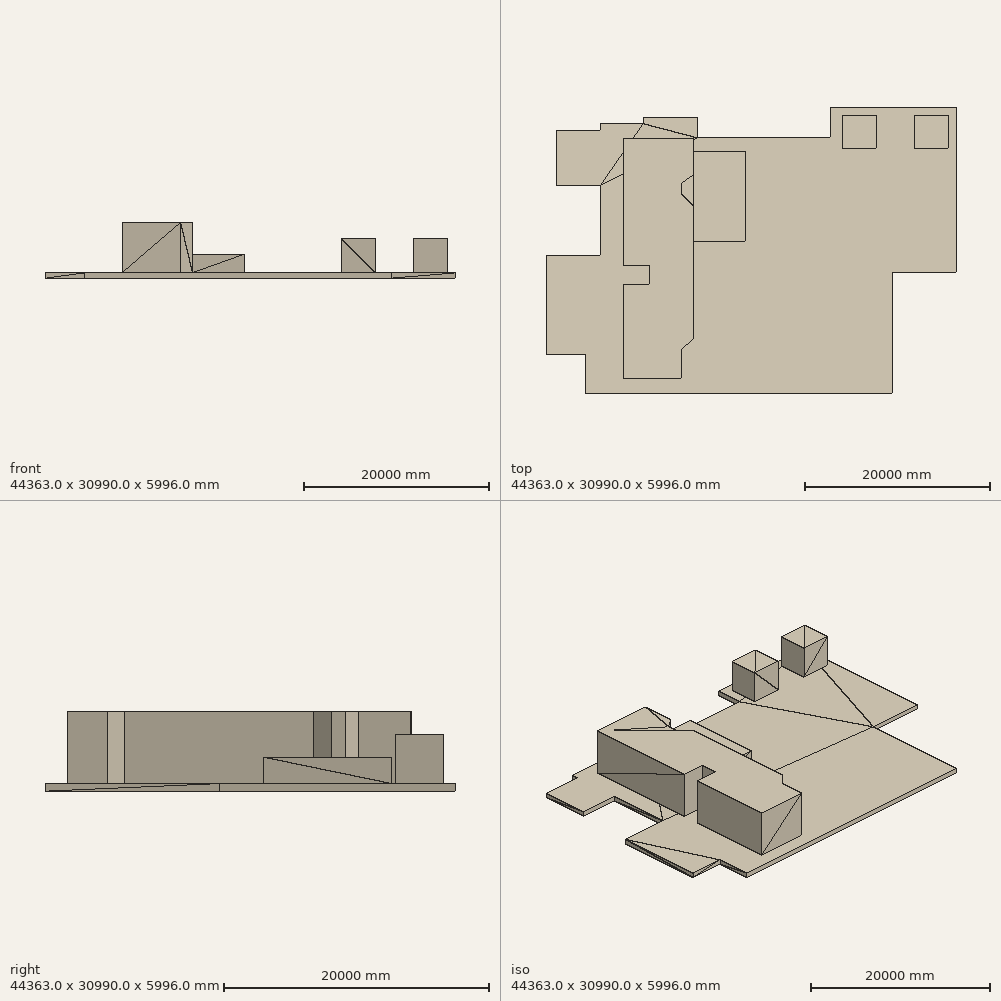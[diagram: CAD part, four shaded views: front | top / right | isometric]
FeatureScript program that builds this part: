
annotation { "Feature Type Name" : "Feature", "Feature Type Description" : "" }
export const myFeature = defineFeature(function(context is Context, id is Id, definition is map)
    precondition{}
    {
        {
            var Q0;
            Q0=qCreatedBy(makeId("Top.planeOp"),FACE);
            var sketch = newSketch(context, id + "F0", { "sketchPlane" : qUnion([Q0])});
            skLineSegment(sketch, "E0", {"start": v(0, 0) * mm, "end": v(39260, 0) * mm, "construction": true});
            skLineSegment(sketch, "E1", {"start": v(0, 0) * mm, "end": v(0, 30290) * mm, "construction": true});
            skLineSegment(sketch, "E2", {"start": v(0, 30290) * mm, "end": v(43730, 30290) * mm, "construction": true});
            skLineSegment(sketch, "E3", {"start": v(6110, 0) * mm, "end": v(39260, 0) * mm});
            skLineSegment(sketch, "E4", {"start": v(39260, 0) * mm, "end": v(39260, 13140) * mm});
            skLineSegment(sketch, "E5", {"start": v(39260, 13140) * mm, "end": v(46240, 13140) * mm});
            skLineSegment(sketch, "E6", {"start": v(46240, 13140) * mm, "end": v(46240, 30990) * mm});
            skLineSegment(sketch, "E7", {"start": v(46240, 30990) * mm, "end": v(32650, 30990) * mm});
            skLineSegment(sketch, "E8", {"start": v(32650, 30990) * mm, "end": v(32650, 27672) * mm});
            skLineSegment(sketch, "E9", {"start": v(32650, 27672) * mm, "end": v(18217, 27672) * mm});
            skLineSegment(sketch, "E10", {"start": v(18217, 27672) * mm, "end": v(18217, 29872) * mm});
            skLineSegment(sketch, "E11", {"start": v(18217, 29872) * mm, "end": v(12367, 29872) * mm});
            skLineSegment(sketch, "E12", {"start": v(12367, 29872) * mm, "end": v(12367, 29207) * mm});
            skLineSegment(sketch, "E13", {"start": v(12367, 29207) * mm, "end": v(7764, 29207) * mm});
            skLineSegment(sketch, "E14", {"start": v(7764, 29207) * mm, "end": v(7764, 28479) * mm});
            skLineSegment(sketch, "E15", {"start": v(7764, 28479) * mm, "end": v(2917, 28479) * mm});
            skLineSegment(sketch, "E16", {"start": v(2917, 28479) * mm, "end": v(2917, 22579) * mm});
            skLineSegment(sketch, "E17", {"start": v(2917, 22579) * mm, "end": v(7764, 22579) * mm});
            skLineSegment(sketch, "E18", {"start": v(7764, 22579) * mm, "end": v(7764, 14932) * mm});
            skLineSegment(sketch, "E19", {"start": v(7764, 14932) * mm, "end": v(1877, 14932) * mm});
            skLineSegment(sketch, "E20", {"start": v(1877, 14932) * mm, "end": v(1877, 4229) * mm});
            skLineSegment(sketch, "E21", {"start": v(1877, 4229) * mm, "end": v(6110, 4229) * mm});
            skLineSegment(sketch, "E22", {"start": v(6110, 4229) * mm, "end": v(6110, 0) * mm});
            skSolve(sketch);
        }
        {
            var Q0;
            Q0=makeQuery(id+"F0.imprint","IMPRINT",FACE,{"disambiguationData":[TD([[makeQuery(id+"F0.imprint","IMPRINT",EDGE,{"derivedFrom":sQuery(id+"F0.wireOp",EDGE,"E3")}),1.0]])]});
            extrude(context, id + "F1", {"entities" : qUnion([Q0]), "depth" : 570 * mm, "offsetDistance" : 25 * mm});
        }
        {
            var Q0;
            Q0=makeQuery(id+"F1.opExtrude","CAP_FACE",FACE,{"disambiguationData":[OSD([sQuery(id+"F0.wireOp",EDGE,"E3"),sQuery(id+"F0.wireOp",EDGE,"E4"),sQuery(id+"F0.wireOp",EDGE,"E5"),sQuery(id+"F0.wireOp",EDGE,"E6"),sQuery(id+"F0.wireOp",EDGE,"E7"),sQuery(id+"F0.wireOp",EDGE,"E8"),sQuery(id+"F0.wireOp",EDGE,"E9"),sQuery(id+"F0.wireOp",EDGE,"E10"),sQuery(id+"F0.wireOp",EDGE,"E11"),sQuery(id+"F0.wireOp",EDGE,"E12"),sQuery(id+"F0.wireOp",EDGE,"E13"),sQuery(id+"F0.wireOp",EDGE,"E14"),sQuery(id+"F0.wireOp",EDGE,"E15"),sQuery(id+"F0.wireOp",EDGE,"E16"),sQuery(id+"F0.wireOp",EDGE,"E17"),sQuery(id+"F0.wireOp",EDGE,"E18"),sQuery(id+"F0.wireOp",EDGE,"E19"),sQuery(id+"F0.wireOp",EDGE,"E20"),sQuery(id+"F0.wireOp",EDGE,"E21"),sQuery(id+"F0.wireOp",EDGE,"E22")])],"isStart":false});
            var sketch = newSketch(context, id + "F2", { "sketchPlane" : qUnion([Q0])});
            skLineSegment(sketch, "E23", {"start": v(0, 0) * mm, "end": v(10434, 0) * mm, "construction": true});
            skLineSegment(sketch, "E24", {"start": v(10434, 0) * mm, "end": v(10434, 1929) * mm, "construction": true});
            skLineSegment(sketch, "E25", {"start": v(16245, 4705) * mm, "end": v(17545, 4705) * mm, "construction": true});
            skLineSegment(sketch, "E26", {"start": v(17545, 4705) * mm, "end": v(17545, 5970) * mm, "construction": true});
            skLineSegment(sketch, "E27", {"start": v(17545, 20175) * mm, "end": v(16195, 20175) * mm, "construction": true});
            skLineSegment(sketch, "E28", {"start": v(16195, 20175) * mm, "end": v(16195, 21500) * mm, "construction": true});
            skLineSegment(sketch, "E29", {"start": v(17545, 20175) * mm, "end": v(16195, 21500) * mm});
            skLineSegment(sketch, "E30", {"start": v(16195, 21500) * mm, "end": v(16195, 22810) * mm, "construction": true});
            skLineSegment(sketch, "E31", {"start": v(16195, 22810) * mm, "end": v(16195, 23790) * mm, "construction": true});
            skLineSegment(sketch, "E32", {"start": v(16195, 23790) * mm, "end": v(17518, 23790) * mm, "construction": true});
            skLineSegment(sketch, "E33", {"start": v(16195, 21500) * mm, "end": v(16195, 22810) * mm});
            skLineSegment(sketch, "E34.0", {"start": v(17795, 5970) * mm, "end": v(17795, 20279.92) * mm});
            skLineSegment(sketch, "E35.0", {"start": v(17795, 20279.92) * mm, "end": v(16445, 21604.92) * mm});
            skLineSegment(sketch, "E36.0", {"start": v(16445, 22684.07) * mm, "end": v(17768, 23664.07) * mm});
            skLineSegment(sketch, "E37.0", {"start": v(17768, 23664.07) * mm, "end": v(17768, 27626) * mm});
            skLineSegment(sketch, "E38.0", {"start": v(17768, 27626) * mm, "end": v(10185, 27626) * mm});
            skLineSegment(sketch, "E39.0", {"start": v(10185, 27626) * mm, "end": v(10185, 13865) * mm});
            skLineSegment(sketch, "E40.0", {"start": v(10185, 11850.03) * mm, "end": v(10183.97, 1679) * mm});
            skLineSegment(sketch, "E41.0", {"start": v(10183.97, 1679) * mm, "end": v(16495, 1679) * mm});
            skLineSegment(sketch, "E42.0", {"start": v(16495, 1679) * mm, "end": v(16495, 4705) * mm});
            skLineSegment(sketch, "E43", {"start": v(16495, 4705) * mm, "end": v(17795, 5970) * mm});
            skLineSegment(sketch, "E44.0", {"start": v(16445, 21604.92) * mm, "end": v(16445, 22684.07) * mm});
            skLineSegment(sketch, "E45", {"start": v(10185, 11850.03) * mm, "end": v(13033, 11850) * mm});
            skLineSegment(sketch, "E46", {"start": v(10185, 13865) * mm, "end": v(13033, 13865) * mm});
            skLineSegment(sketch, "E47", {"start": v(13033, 13865) * mm, "end": v(13033, 11850) * mm});
            skSolve(sketch);
        }
        {
            var Q0;
            Q0=makeQuery(id+"F2.imprint","IMPRINT",FACE,{"disambiguationData":[TD([[makeQuery(id+"F2.imprint","IMPRINT",EDGE,{"derivedFrom":sQuery(id+"F2.wireOp",EDGE,"E34.0")}),1.0]])]});
            extrude(context, id + "F3", {"entities" : qUnion([Q0]), "depth" : 5426 * mm, "offsetDistance" : 25 * mm});
        }
        {
            var Q0;
            Q0=makeQuery(id+"F1.opExtrude","CAP_FACE",FACE,{"disambiguationData":[OSD([sQuery(id+"F0.wireOp",EDGE,"E3"),sQuery(id+"F0.wireOp",EDGE,"E4"),sQuery(id+"F0.wireOp",EDGE,"E5"),sQuery(id+"F0.wireOp",EDGE,"E6"),sQuery(id+"F0.wireOp",EDGE,"E7"),sQuery(id+"F0.wireOp",EDGE,"E8"),sQuery(id+"F0.wireOp",EDGE,"E9"),sQuery(id+"F0.wireOp",EDGE,"E10"),sQuery(id+"F0.wireOp",EDGE,"E11"),sQuery(id+"F0.wireOp",EDGE,"E12"),sQuery(id+"F0.wireOp",EDGE,"E13"),sQuery(id+"F0.wireOp",EDGE,"E14"),sQuery(id+"F0.wireOp",EDGE,"E15"),sQuery(id+"F0.wireOp",EDGE,"E16"),sQuery(id+"F0.wireOp",EDGE,"E17"),sQuery(id+"F0.wireOp",EDGE,"E18"),sQuery(id+"F0.wireOp",EDGE,"E19"),sQuery(id+"F0.wireOp",EDGE,"E20"),sQuery(id+"F0.wireOp",EDGE,"E21"),sQuery(id+"F0.wireOp",EDGE,"E22")])],"isStart":false});
            var sketch = newSketch(context, id + "F4", { "sketchPlane" : qUnion([Q0])});
            skLineSegment(sketch, "E48", {"start": v(18217, 27672) * mm, "end": v(18217, 26179) * mm, "construction": true});
            skLineSegment(sketch, "E49", {"start": v(17764.64, 26179) * mm, "end": v(23364.64, 26179) * mm});
            skLineSegment(sketch, "E50", {"start": v(23364.64, 26179) * mm, "end": v(23364.64, 16489) * mm});
            skLineSegment(sketch, "E51", {"start": v(23364.64, 16489) * mm, "end": v(17764.64, 16489) * mm});
            skLineSegment(sketch, "E52", {"start": v(17764.64, 16489) * mm, "end": v(17764.64, 26179) * mm});
            skSolve(sketch);
        }
        {
            var Q0;
            Q0=makeQuery(id+"F4.imprint","IMPRINT",FACE,{"disambiguationData":[TD([[makeQuery(id+"F4.imprint","IMPRINT",EDGE,{"derivedFrom":sQuery(id+"F4.wireOp",EDGE,"E49")}),-1.0]])]});
            extrude(context, id + "F5", {"entities" : qUnion([Q0]), "depth" : 2000 * mm, "offsetDistance" : 25 * mm});
        }
        {
            var Q0;
            Q0=makeQuery(id+"F1.opExtrude","CAP_FACE",FACE,{"disambiguationData":[OSD([sQuery(id+"F0.wireOp",EDGE,"E3"),sQuery(id+"F0.wireOp",EDGE,"E4"),sQuery(id+"F0.wireOp",EDGE,"E5"),sQuery(id+"F0.wireOp",EDGE,"E6"),sQuery(id+"F0.wireOp",EDGE,"E7"),sQuery(id+"F0.wireOp",EDGE,"E8"),sQuery(id+"F0.wireOp",EDGE,"E9"),sQuery(id+"F0.wireOp",EDGE,"E10"),sQuery(id+"F0.wireOp",EDGE,"E11"),sQuery(id+"F0.wireOp",EDGE,"E12"),sQuery(id+"F0.wireOp",EDGE,"E13"),sQuery(id+"F0.wireOp",EDGE,"E14"),sQuery(id+"F0.wireOp",EDGE,"E15"),sQuery(id+"F0.wireOp",EDGE,"E16"),sQuery(id+"F0.wireOp",EDGE,"E17"),sQuery(id+"F0.wireOp",EDGE,"E18"),sQuery(id+"F0.wireOp",EDGE,"E19"),sQuery(id+"F0.wireOp",EDGE,"E20"),sQuery(id+"F0.wireOp",EDGE,"E21"),sQuery(id+"F0.wireOp",EDGE,"E22")])],"isStart":false});
            var sketch = newSketch(context, id + "F6", { "sketchPlane" : qUnion([Q0])});
            skLineSegment(sketch, "E53", {"start": v(46240, 30990) * mm, "end": v(46240, 30090) * mm, "construction": true});
            skLineSegment(sketch, "E54", {"start": v(46240, 30090) * mm, "end": v(45358, 30090) * mm, "construction": true});
            skLineSegment(sketch, "E55", {"start": v(45358, 30090) * mm, "end": v(41658, 30090) * mm});
            skLineSegment(sketch, "E56", {"start": v(41658, 30090) * mm, "end": v(41658, 26490) * mm});
            skLineSegment(sketch, "E57", {"start": v(41658, 26490) * mm, "end": v(45358, 26490) * mm});
            skLineSegment(sketch, "E58", {"start": v(45358, 26490) * mm, "end": v(45358, 30090) * mm});
            skLineSegment(sketch, "E59", {"start": v(46240, 30090) * mm, "end": v(37585, 30090) * mm, "construction": true});
            skLineSegment(sketch, "E60", {"start": v(37585, 30090) * mm, "end": v(33885, 30090) * mm});
            skLineSegment(sketch, "E61", {"start": v(37585, 30090) * mm, "end": v(37585, 26490) * mm});
            skLineSegment(sketch, "E62", {"start": v(37585, 26490) * mm, "end": v(33885, 26490) * mm});
            skLineSegment(sketch, "E63", {"start": v(33885, 26490) * mm, "end": v(33885, 30090) * mm});
            skSolve(sketch);
        }
        {
            var Q0;
            Q0=makeQuery(id+"F6.imprint","IMPRINT",FACE,{"disambiguationData":[TD([[makeQuery(id+"F6.imprint","IMPRINT",EDGE,{"derivedFrom":sQuery(id+"F6.wireOp",EDGE,"E55")}),1.0]])]});
            var Q1;
            Q1=makeQuery(id+"F6.imprint","IMPRINT",FACE,{"disambiguationData":[TD([[makeQuery(id+"F6.imprint","IMPRINT",EDGE,{"derivedFrom":sQuery(id+"F6.wireOp",EDGE,"E60")}),1.0]])]});
            extrude(context, id + "F7", {"entities" : qUnion([Q0, Q1]), "depth" : 3700 * mm, "offsetDistance" : 25 * mm});
        }
    });
